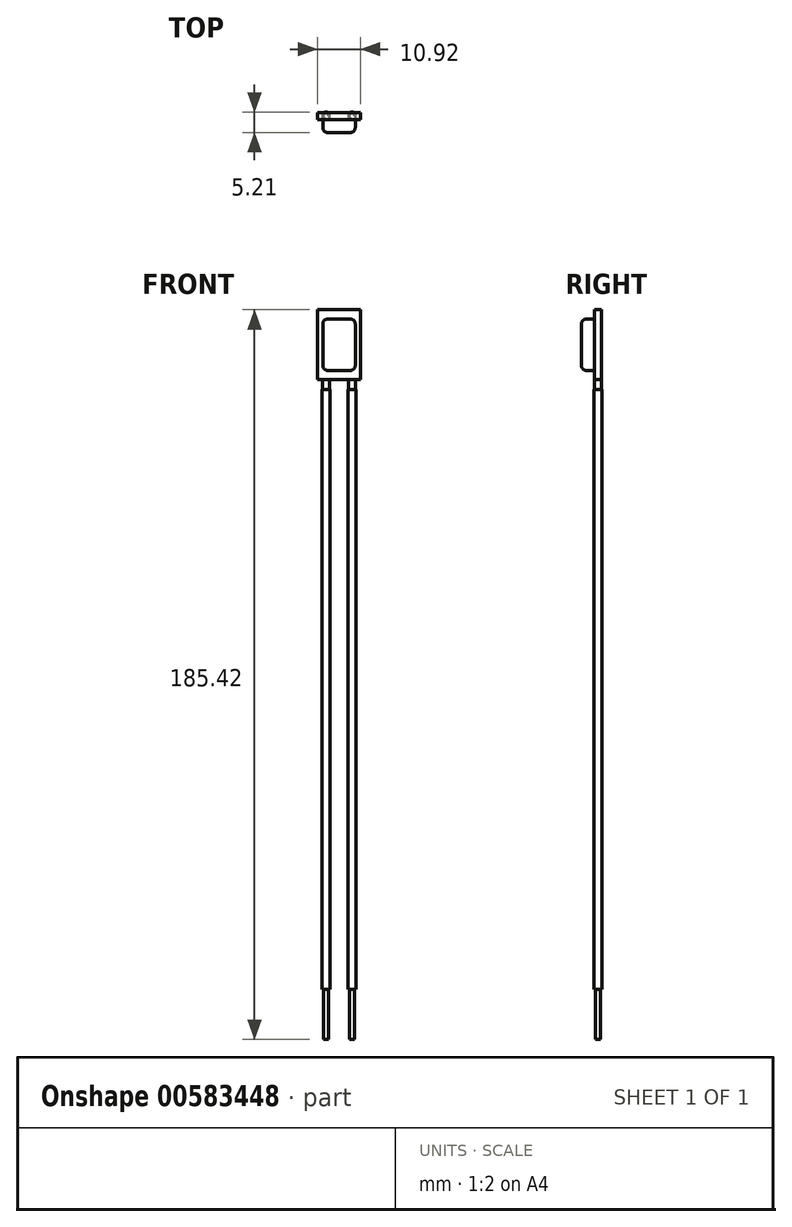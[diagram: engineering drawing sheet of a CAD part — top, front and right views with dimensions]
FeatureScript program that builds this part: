
annotation { "Feature Type Name" : "Feature", "Feature Type Description" : "" }
export const myFeature = defineFeature(function(context is Context, id is Id, definition is map)
    precondition{}
    {
        {
            var Q0;
            Q0=qCreatedBy(makeId("Front.planeOp"),FACE);
            var sketch = newSketch(context, id + "F0", { "sketchPlane" : qUnion([Q0])});
            skLineSegment(sketch, "E0.bottom", {"start": v(5.46, -8.9) * mm, "end": v(-5.46, -8.9) * mm});
            skLineSegment(sketch, "E0.top", {"start": v(5.46, 8.9) * mm, "end": v(-5.46, 8.9) * mm});
            skLineSegment(sketch, "E0.left", {"start": v(5.46, -8.9) * mm, "end": v(5.46, 8.9) * mm});
            skLineSegment(sketch, "E0.right", {"start": v(-5.46, -8.9) * mm, "end": v(-5.46, 8.89) * mm});
            skPoint(sketch, "E0.middle", {"position": v(0, 0) * mm});
            skSolve(sketch);
        }
        {
            var Q0;
            Q0=makeQuery(id+"F0.imprint","IMPRINT",FACE,{"disambiguationData":[TD([[makeQuery(id+"F0.imprint","IMPRINT",EDGE,{"derivedFrom":sQuery(id+"F0.wireOp",EDGE,"E0.bottom")}),-1.0]])]});
            extrude(context, id + "F1", {"entities" : qUnion([Q0]), "depth" : 1.78 * mm});
        }
        {
            var Q0;
            Q0=makeQuery(id+"F1.opExtrude","CAP_FACE",FACE,{"disambiguationData":[OSD([sQuery(id+"F0.wireOp",EDGE,"E0.bottom"),sQuery(id+"F0.wireOp",EDGE,"E0.top"),sQuery(id+"F0.wireOp",EDGE,"E0.left"),sQuery(id+"F0.wireOp",EDGE,"E0.right")])],"isStart":false});
            var sketch = newSketch(context, id + "F2", { "sketchPlane" : qUnion([Q0])});
            skLineSegment(sketch, "E1.bottom", {"start": v(4.13, -6.54) * mm, "end": v(-4.13, -6.54) * mm});
            skLineSegment(sketch, "E1.top", {"start": v(4.13, 6.54) * mm, "end": v(-4.13, 6.54) * mm});
            skLineSegment(sketch, "E1.left", {"start": v(4.13, -6.54) * mm, "end": v(4.13, 6.54) * mm});
            skLineSegment(sketch, "E1.right", {"start": v(-4.13, -6.54) * mm, "end": v(-4.13, 6.54) * mm});
            skPoint(sketch, "E1.middle", {"position": v(0, 0) * mm});
            skSolve(sketch);
        }
        {
            var Q0;
            Q0=makeQuery(id+"F2.imprint","IMPRINT",FACE,{"disambiguationData":[TD([[makeQuery(id+"F2.imprint","IMPRINT",EDGE,{"derivedFrom":sQuery(id+"F2.wireOp",EDGE,"E1.bottom")}),-1.0]])]});
            extrude(context, id + "F3", {"entities" : qUnion([Q0]), "operationType" : NewBodyOperationType.ADD, "depth" : 3.3 * mm});
        }
        {
            var Q0;
            Q0=makeQuery(id+"F3.opExtrude","CAP_EDGE",EDGE,{"disambiguationData":[OSD([sQuery(id+"F2.wireOp",EDGE,"E1.right")])],"isStart":false});
            var Q1;
            Q1=makeQuery(id+"F3.opExtrude","CAP_EDGE",EDGE,{"disambiguationData":[OSD([sQuery(id+"F2.wireOp",EDGE,"E1.top")])],"isStart":false});
            var Q2;
            Q2=makeQuery(id+"F3.opExtrude","CAP_EDGE",EDGE,{"disambiguationData":[OSD([sQuery(id+"F2.wireOp",EDGE,"E1.left")])],"isStart":false});
            var Q3;
            Q3=makeQuery(id+"F3.opExtrude","CAP_EDGE",EDGE,{"disambiguationData":[OSD([sQuery(id+"F2.wireOp",EDGE,"E1.bottom")])],"isStart":false});
            var Q4;
            Q4=makeQuery(id+"F3.opExtrude","SWEPT_EDGE",EDGE,{"disambiguationData":[OSD([sQuery(id+"F2.wireOp",EDGE,"E1.bottom"),sQuery(id+"F2.wireOp",EDGE,"E1.right")])]});
            var Q5;
            Q5=makeQuery(id+"F3.opExtrude","SWEPT_EDGE",EDGE,{"disambiguationData":[OSD([sQuery(id+"F2.wireOp",EDGE,"E1.top"),sQuery(id+"F2.wireOp",EDGE,"E1.right")])]});
            var Q6;
            Q6=makeQuery(id+"F3.opExtrude","SWEPT_EDGE",EDGE,{"disambiguationData":[OSD([sQuery(id+"F2.wireOp",EDGE,"E1.top"),sQuery(id+"F2.wireOp",EDGE,"E1.left")])]});
            var Q7;
            Q7=makeQuery(id+"F3.opExtrude","SWEPT_EDGE",EDGE,{"disambiguationData":[OSD([sQuery(id+"F2.wireOp",EDGE,"E1.bottom"),sQuery(id+"F2.wireOp",EDGE,"E1.left")])]});
            fillet(context, id + "F4", {"entities" : qUnion([Q0, Q1, Q2, Q3, Q4, Q5, Q6, Q7]), "radius" : 1.27 * mm, "tangentPropagation" : true, "allowEdgeOverflow" : false});
        }
        {
            var Q0;
            Q0=makeQuery(id+"F1.opExtrude","SWEPT_FACE",FACE,{"disambiguationData":[OSD([sQuery(id+"F0.wireOp",EDGE,"E0.bottom")])]});
            var sketch = newSketch(context, id + "F5", { "sketchPlane" : qUnion([Q0])});
            skCircle(sketch, "E2", {"center": v(-3.3, 0.89) * mm, "radius": 0.89 * mm});
            skPoint(sketch, "E2.centerSnap0", {"position": v(-5.46, 0.89) * mm});
            skCircle(sketch, "E3", {"center": v(3.3, 0.89) * mm, "radius": 0.89 * mm});
            skPoint(sketch, "E3.centerSnap0", {"position": v(5.46, 0.89) * mm});
            skSolve(sketch);
        }
        {
            var Q0;
            Q0=qSketchRegion(id+"F5",true);
            extrude(context, id + "F6", {"entities" : qUnion([Q0]), "operationType" : NewBodyOperationType.ADD, "depth" : 2.54 * mm});
        }
        {
            var Q0;
            Q0=makeQuery(id+"F6.opExtrude","CAP_FACE",FACE,{"disambiguationData":[OSD([sQuery(id+"F5.wireOp",EDGE,"E2")])],"isStart":false});
            var sketch = newSketch(context, id + "F7", { "sketchPlane" : qUnion([Q0])});
            skCircle(sketch, "E4", {"center": v(-3.3, 0.89) * mm, "radius": 1.02 * mm});
            skSolve(sketch);
        }
        {
            var Q0;
            Q0=qSketchRegion(id+"F7",true);
            extrude(context, id + "F8", {"entities" : qUnion([Q0]), "depth" : 152.4 * mm, "offsetDistance" : 25.4 * mm});
        }
        {
            var Q0;
            Q0=makeQuery(id+"F6.opExtrude","CAP_FACE",FACE,{"disambiguationData":[OSD([sQuery(id+"F5.wireOp",EDGE,"E3")])],"isStart":false});
            var sketch = newSketch(context, id + "F9", { "sketchPlane" : qUnion([Q0])});
            skCircle(sketch, "E5", {"center": v(3.3, 0.89) * mm, "radius": 1.02 * mm});
            skSolve(sketch);
        }
        {
            var Q0;
            Q0=qSketchRegion(id+"F9",true);
            extrude(context, id + "F10", {"entities" : qUnion([Q0]), "depth" : 152.4 * mm, "offsetDistance" : 25.4 * mm});
        }
        {
            var Q0;
            Q0=makeQuery(id+"F8.opExtrude","CAP_FACE",FACE,{"disambiguationData":[OSD([sQuery(id+"F7.wireOp",EDGE,"E4")])],"isStart":false});
            var sketch = newSketch(context, id + "F11", { "sketchPlane" : qUnion([Q0])});
            skCircle(sketch, "E6", {"center": v(-3.3, 0.89) * mm, "radius": 0.6 * mm});
            skSolve(sketch);
        }
        {
            var Q0;
            Q0=qSketchRegion(id+"F11",true);
            extrude(context, id + "F12", {"entities" : qUnion([Q0]), "depth" : 12.7 * mm});
        }
        {
            var Q0;
            Q0=makeQuery(id+"F10.opExtrude","CAP_FACE",FACE,{"disambiguationData":[OSD([sQuery(id+"F9.wireOp",EDGE,"E5")])],"isStart":false});
            var sketch = newSketch(context, id + "F13", { "sketchPlane" : qUnion([Q0])});
            skCircle(sketch, "E7", {"center": v(3.3, 0.89) * mm, "radius": 0.6 * mm});
            skSolve(sketch);
        }
        {
            var Q0;
            Q0=qSketchRegion(id+"F13",true);
            extrude(context, id + "F14", {"entities" : qUnion([Q0]), "depth" : 12.7 * mm});
        }
    });
